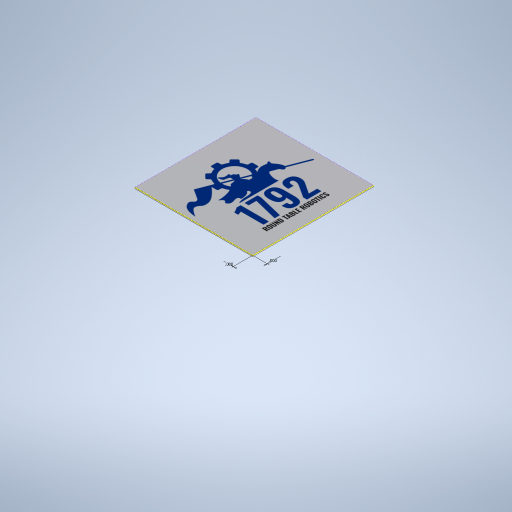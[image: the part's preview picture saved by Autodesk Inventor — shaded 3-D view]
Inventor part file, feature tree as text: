
AUTODESK INVENTOR PART (.ipt)
format: ipt  version: 2023 (Build 270158000, 158)  size: 276,992 bytes
history: native  units: in
note: dims shown in document units (in); Inventor stores cm internally (conversion verified against a paired STEP export)
features: sketch x2, other x2, sheet_metal_op x1
ambient origin geometry x8: Origin, YZ Plane, XZ Plane, XY Plane, X Axis, Y Axis, Z Axis, Center Point
bodies: Solid1 (feature_tree)
feature tree (5):
  sheet_metal_op  "Face1"
  sketch  "Sketch2"  dims[d59=12.0in d60=12.3402in d63=0.0in d64=0.0in]
  sketch  "Sketch1"  dims[d58=0.12in]
  other  "Plate1"
  other  "Image2"
